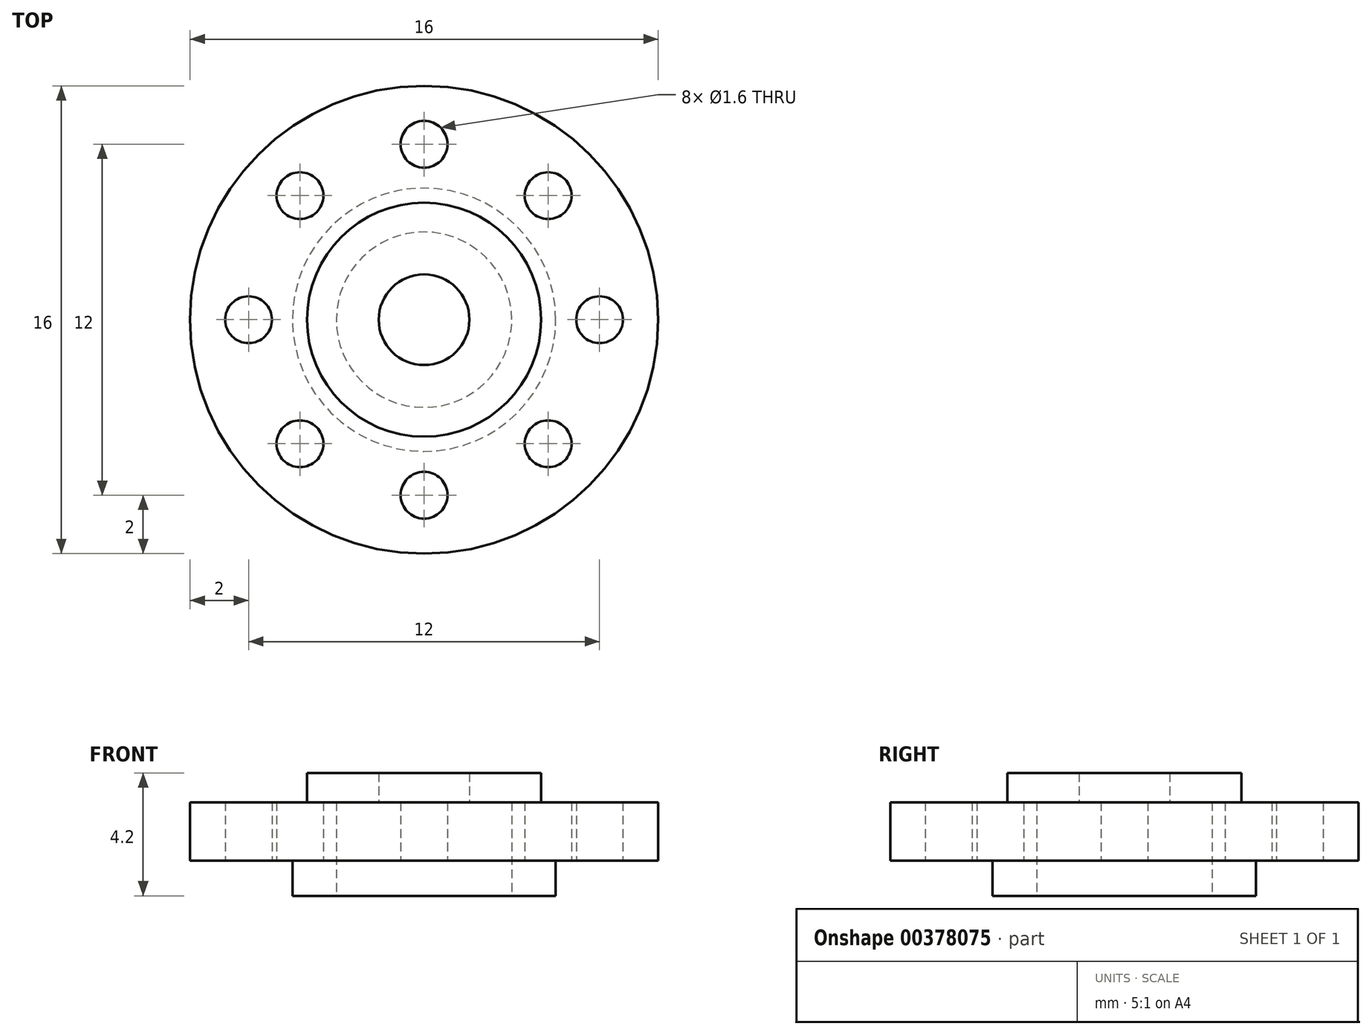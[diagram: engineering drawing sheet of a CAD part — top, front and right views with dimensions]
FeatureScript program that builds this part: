
annotation { "Feature Type Name" : "Feature", "Feature Type Description" : "" }
export const myFeature = defineFeature(function(context is Context, id is Id, definition is map)
    precondition{}
    {
        {
            var Q0;
            Q0=qCreatedBy(makeId("Top.planeOp"),FACE);
            var sketch = newSketch(context, id + "F0", { "sketchPlane" : qUnion([Q0])});
            skCircle(sketch, "E0", {"center": v(0, 0) * mm, "radius": 3 * mm});
            skCircle(sketch, "E1", {"center": v(0, 0) * mm, "radius": 4.5 * mm});
            skSolve(sketch);
        }
        {
            var Q0;
            Q0=makeQuery(id+"F0.imprint","IMPRINT",FACE,{"disambiguationData":[TD([[makeQuery(id+"F0.imprint","IMPRINT",EDGE,{"derivedFrom":sQuery(id+"F0.wireOp",EDGE,"E0")}),-1.0]])]});
            extrude(context, id + "F1", {"entities" : qUnion([Q0]), "depth" : (3.2 - 2) * mm});
        }
        {
            var Q0;
            Q0=makeQuery(id+"F1.opExtrude","CAP_FACE",FACE,{"disambiguationData":[OSD([sQuery(id+"F0.wireOp",EDGE,"E0"),sQuery(id+"F0.wireOp",EDGE,"E1")])],"isStart":false});
            var sketch = newSketch(context, id + "F2", { "sketchPlane" : qUnion([Q0])});
            skCircle(sketch, "E2", {"center": v(0, 0) * mm, "radius": 8 * mm});
            skCircle(sketch, "E3.0", {"center": v(0, 0) * mm, "radius": 3 * mm});
            skLineSegment(sketch, "E4", {"start": v(0, 0) * mm, "end": v(0, 6) * mm, "construction": true});
            skCircle(sketch, "E5", {"center": v(0, 6) * mm, "radius": 0.8 * mm});
            skCircle(sketch, "E6.1.0", {"center": v(-4.24, 4.24) * mm, "radius": 0.8 * mm});
            skCircle(sketch, "E6.2.0", {"center": v(-6, 0) * mm, "radius": 0.8 * mm});
            skCircle(sketch, "E6.3.0", {"center": v(-4.24, -4.24) * mm, "radius": 0.8 * mm});
            skCircle(sketch, "E6.4.0", {"center": v(0, -6) * mm, "radius": 0.8 * mm});
            skCircle(sketch, "E6.5.0", {"center": v(4.24, -4.24) * mm, "radius": 0.8 * mm});
            skCircle(sketch, "E6.6.0", {"center": v(6, 0) * mm, "radius": 0.8 * mm});
            skCircle(sketch, "E6.7.0", {"center": v(4.24, 4.24) * mm, "radius": 0.8 * mm});
            skSolve(sketch);
        }
        {
            var Q0;
            Q0=makeQuery(id+"F2.imprint","IMPRINT",FACE,{"disambiguationData":[TD([[makeQuery(id+"F2.imprint","IMPRINT",EDGE,{"derivedFrom":sQuery(id+"F2.wireOp",EDGE,"E3.0")}),-1.0]])]});
            var Q1;
            Q1=makeQuery(id+"F2.imprint","IMPRINT",FACE,{"disambiguationData":[TD([[makeQuery(id+"F2.imprint","IMPRINT",EDGE,{"derivedFrom":sQuery(id+"F2.wireOp",EDGE,"E2")}),1.0]])]});
            extrude(context, id + "F3", {"entities" : qUnion([Q0, Q1]), "operationType" : NewBodyOperationType.ADD, "depth" : 2 * mm});
        }
        {
            var Q0;
            Q0=makeQuery(id+"F3.opExtrude","CAP_FACE",FACE,{"disambiguationData":[OSD([sQuery(id+"F2.wireOp",EDGE,"E2"),sQuery(id+"F2.wireOp",EDGE,"E3.0"),sQuery(id+"F2.wireOp",EDGE,"E5"),sQuery(id+"F2.wireOp",EDGE,"E6.1.0"),sQuery(id+"F2.wireOp",EDGE,"E6.2.0"),sQuery(id+"F2.wireOp",EDGE,"E6.3.0"),sQuery(id+"F2.wireOp",EDGE,"E6.4.0"),sQuery(id+"F2.wireOp",EDGE,"E6.5.0"),sQuery(id+"F2.wireOp",EDGE,"E6.6.0"),sQuery(id+"F2.wireOp",EDGE,"E6.7.0")])],"isStart":false});
            var sketch = newSketch(context, id + "F4", { "sketchPlane" : qUnion([Q0])});
            skCircle(sketch, "E7", {"center": v(0, 0) * mm, "radius": 1.55 * mm});
            skCircle(sketch, "E8", {"center": v(0, 0) * mm, "radius": 4 * mm});
            skSolve(sketch);
        }
        {
            var Q0;
            Q0=qSketchRegion(id+"F4",true);
            extrude(context, id + "F5", {"entities" : qUnion([Q0]), "operationType" : NewBodyOperationType.ADD, "depth" : 1 * mm});
        }
    });
